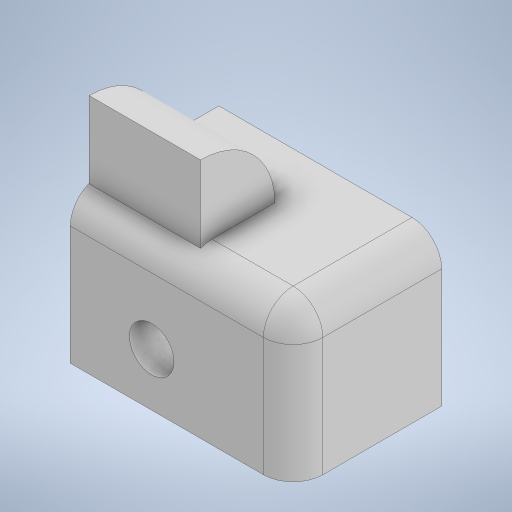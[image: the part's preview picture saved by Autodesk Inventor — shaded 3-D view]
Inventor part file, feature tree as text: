
AUTODESK INVENTOR PART (.ipt)
format: ipt  version: 2023.2 (Build 272271000, 271)  size: 231,936 bytes
history: native  units: mm
features: sketch x3, extrude x1, revolve x1, fillet x1, hole x1
ambient origin geometry x8: Origin, YZ Plane, XZ Plane, XY Plane, X Axis, Y Axis, Z Axis, Center Point
bodies: Solid1 (feature_tree)
feature tree (7):
  extrude  "Extrusion1"  Depth=15.0mm
  revolve  "Revolution1"  [1 undecoded]
  fillet  "Fillet1"  Radius=7.5mm
  hole  "Hole1"  [1 undecoded]
  sketch  "Sketch1"  dims[d0=10.0mm d1=15.0mm]
  sketch  "Sketch2"  dims[d2=10.0mm d3=0.0mm d4=5.0mm d5=7.5mm]
  sketch  "Sketch3"  dims[d6=90.0deg d7=2.0mm d8=3.0mm d9=6.0mm d10=4.0mm d11=2.0mm d12=90.0deg d13=8.0mm d14=20.594885mm]
note: 2 required parameter values undecoded (feature->parameter linkage not recoverable at this tier; creation-order binding heuristic only, values carry confidence <= 0.55)